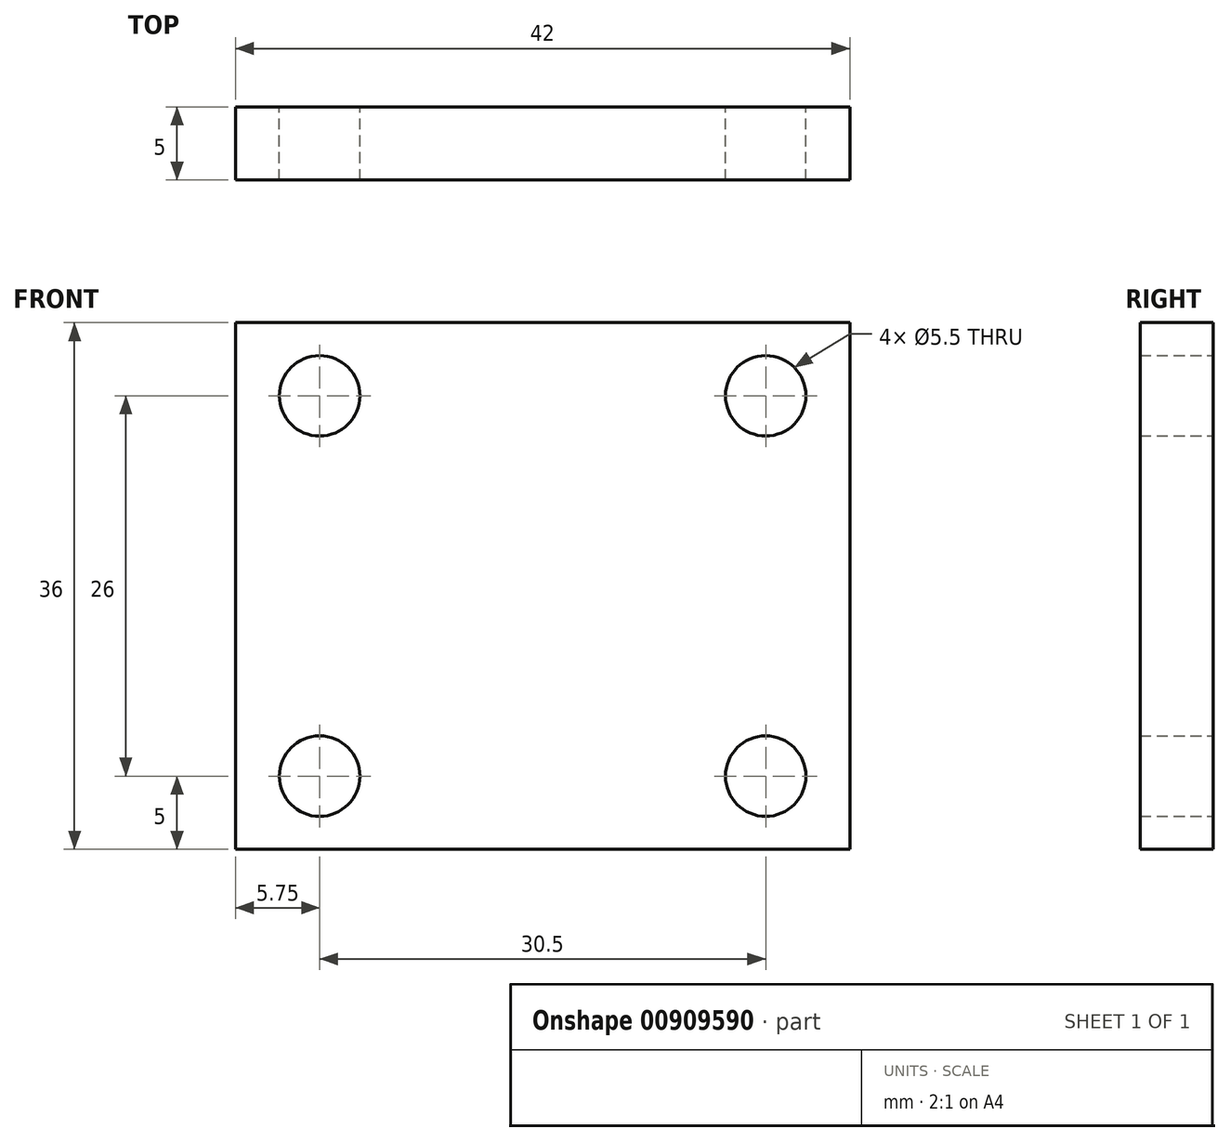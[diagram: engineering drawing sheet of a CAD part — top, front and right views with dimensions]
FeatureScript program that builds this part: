
annotation { "Feature Type Name" : "Feature", "Feature Type Description" : "" }
export const myFeature = defineFeature(function(context is Context, id is Id, definition is map)
    precondition{}
    {
        {
            var Q0;
            Q0=qCreatedBy(makeId("Front.planeOp"),FACE);
            var sketch = newSketch(context, id + "F0", { "sketchPlane" : qUnion([Q0])});
            skLineSegment(sketch, "E0.bottom", {"start": v(21, 18) * mm, "end": v(-21, 18) * mm});
            skLineSegment(sketch, "E0.top", {"start": v(21, -18) * mm, "end": v(-21, -18) * mm});
            skLineSegment(sketch, "E0.left", {"start": v(21, 18) * mm, "end": v(21, -18) * mm});
            skLineSegment(sketch, "E0.right", {"start": v(-21, 18) * mm, "end": v(-21, -18) * mm});
            skPoint(sketch, "E0.middle", {"position": v(0, 0) * mm});
            skLineSegment(sketch, "E1", {"start": v(0, 18) * mm, "end": v(0, -18) * mm, "construction": true});
            skLineSegment(sketch, "E2", {"start": v(-21, 0) * mm, "end": v(21, 0) * mm, "construction": true});
            skCircle(sketch, "E3", {"center": v(-15.25, 13) * mm, "radius": 2.75 * mm});
            skCircle(sketch, "E4.MirrorC", {"center": v(15.25, 13) * mm, "radius": 2.75 * mm});
            skCircle(sketch, "E5.MirrorC", {"center": v(-15.25, -13) * mm, "radius": 2.75 * mm});
            skCircle(sketch, "E6.MirrorC", {"center": v(15.25, -13) * mm, "radius": 2.75 * mm});
            skSolve(sketch);
        }
        {
            var Q0;
            Q0=makeQuery(id+"F0.imprint","IMPRINT",FACE,{"disambiguationData":[TD([[makeQuery(id+"F0.imprint","IMPRINT",EDGE,{"derivedFrom":sQuery(id+"F0.wireOp",EDGE,"E0.bottom")}),1.0]])]});
            extrude(context, id + "F1", {"entities" : qUnion([Q0]), "depth" : 5 * mm, "offsetDistance" : 25.4 * mm});
        }
    });
